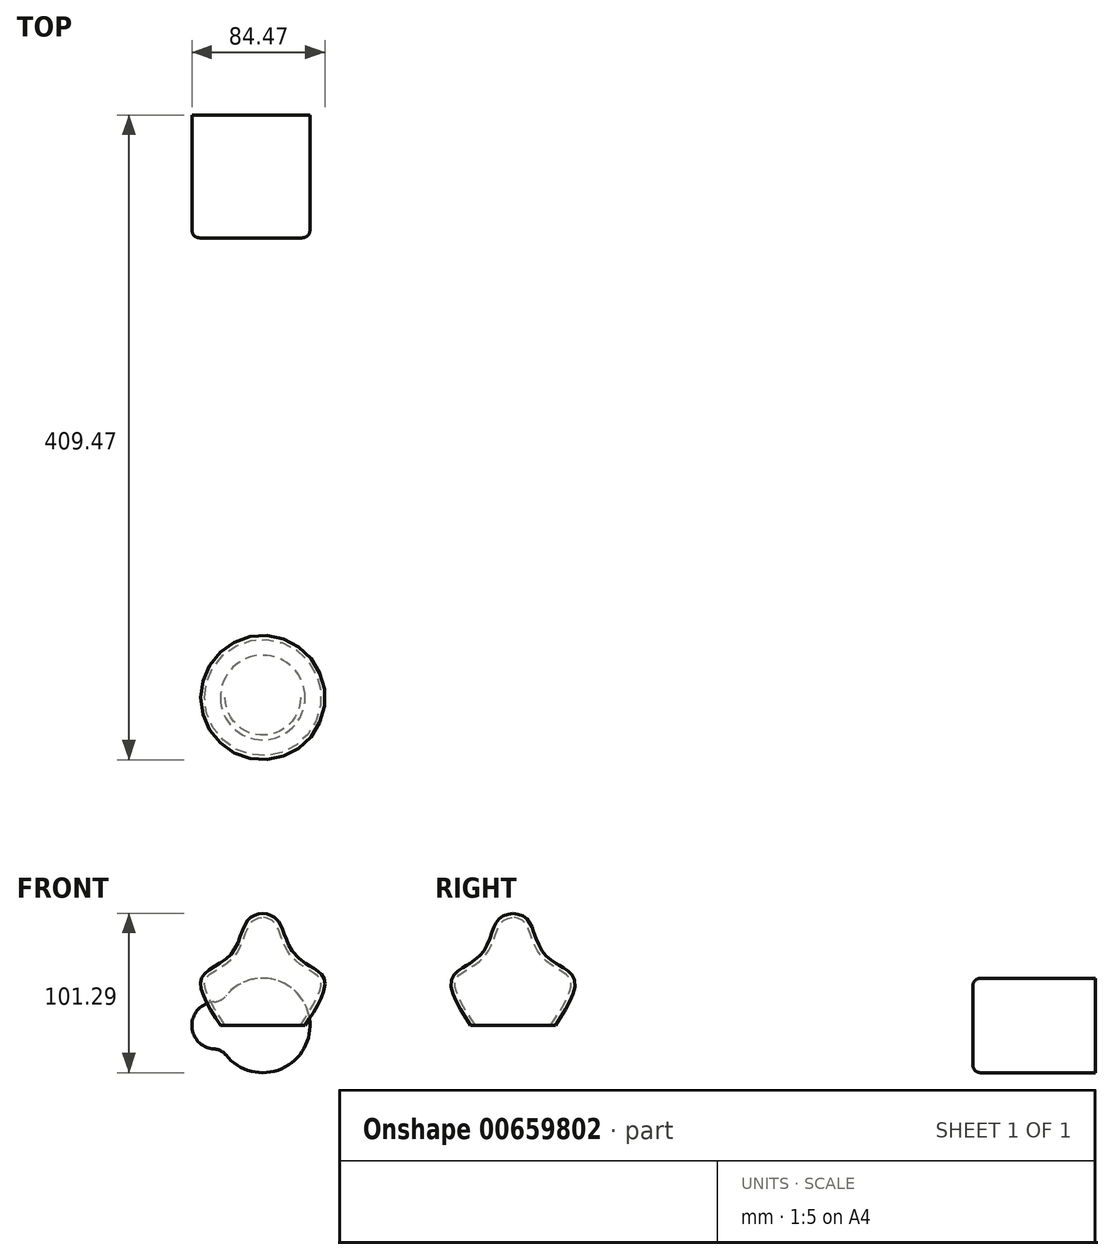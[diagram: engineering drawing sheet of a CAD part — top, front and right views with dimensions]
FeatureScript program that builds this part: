
annotation { "Feature Type Name" : "Feature", "Feature Type Description" : "" }
export const myFeature = defineFeature(function(context is Context, id is Id, definition is map)
    precondition{}
    {
        {
            var Q0;
            Q0=qCreatedBy(makeId("Front.planeOp"),FACE);
            var sketch = newSketch(context, id + "F0", { "sketchPlane" : qUnion([Q0])});
            skArc(sketch, "E0", {"start": v(-23.44, -18.73) * mm, "mid": v(30, 0) * mm, "end": v(-23.44, 18.73) * mm});
            skArc(sketch, "E1", {"start": v(-30.75, 14.98) * mm, "mid": v(-45, 0) * mm, "end": v(-30.75, -14.98) * mm});
            skPoint(sketch, "E2.visualSharp", {"position": v(-26.25, 14.52) * mm});
            skArc(sketch, "E2.filletArc", {"start": v(-30.75, 14.98) * mm, "mid": v(-26.7, 16.07) * mm, "end": v(-23.44, 18.73) * mm});
            skPoint(sketch, "E3.visualSharp", {"position": v(-26.25, -14.52) * mm});
            skArc(sketch, "E3.filletArc", {"start": v(-23.44, -18.73) * mm, "mid": v(-26.7, -16.07) * mm, "end": v(-30.75, -14.98) * mm});
            skSolve(sketch);
        }
        {
            var Q0;
            Q0=makeQuery(id+"F0.imprint","IMPRINT",FACE,{"disambiguationData":[TD([[makeQuery(id+"F0.imprint","IMPRINT",EDGE,{"derivedFrom":sQuery(id+"F0.wireOp",EDGE,"E0")}),1.0]])]});
            extrude(context, id + "F1", {"entities" : qUnion([Q0]), "oppositeDirection" : true, "depth" : 78 * mm, "offsetDistance" : 25 * mm});
        }
        {
            var Q0;
            Q0=makeQuery(id+"F1.opExtrude","CAP_EDGE",EDGE,{"disambiguationData":[OSD([sQuery(id+"F0.wireOp",EDGE,"E0")])],"isStart":true});
            fillet(context, id + "F2", {"entities" : qUnion([Q0]), "radius" : 5 * mm, "tangentPropagation" : true, "allowEdgeOverflow" : false});
        }
        {
            var Q0;
            Q0=qCreatedBy(makeId("Right.planeOp"),FACE);
            cPlane(context, id + "F3", {"entities" : qUnion([Q0]), "cplaneType" : CPlaneType.OFFSET, "offset" : 154 * mm, "width" : 150 * mm, "height" : 150 * mm});
        }
        {
            var Q0;
            Q0=qCreatedBy(id+"F3.planeOp",FACE);
            cPlane(context, id + "F4", {"entities" : qUnion([Q0]), "cplaneType" : CPlaneType.OFFSET, "offset" : 120 * mm, "width" : 150 * mm, "height" : 150 * mm});
        }
        {
            var Q0;
            Q0=qCreatedBy(makeId("Front.planeOp"),FACE);
            cPlane(context, id + "F5", {"entities" : qUnion([Q0]), "cplaneType" : CPlaneType.OFFSET, "offset" : 292 * mm, "width" : 150 * mm, "height" : 150 * mm});
        }
        {
            var Q0;
            Q0=qCreatedBy(id+"F5.planeOp",FACE);
            var sketch = newSketch(context, id + "F6", { "sketchPlane" : qUnion([Q0])});
            skFitSpline(sketch, "E4", {"points": [v(-26.88, 0) * mm, v(-38.8, 30.05) * mm, v(-20.42, 44.96) * mm, v(-9.73, 66.57) * mm, v(0, 71.3) * mm], "startDerivative": vector(-73.65, 114.28) * mm, "endDerivative": vector(61.92, 12.77) * mm});
            skLineSegment(sketch, "E5", {"start": v(0, 71.3) * mm, "end": v(0, 0) * mm});
            skLineSegment(sketch, "E6", {"start": v(0, 0) * mm, "end": v(-26.88, 0) * mm});
            skLineSegment(sketch, "E7", {"start": v(0, 0) * mm, "end": v(0, -43.5) * mm, "construction": true});
            skSolve(sketch);
        }
        {
            var Q0;
            Q0=makeQuery(id+"F6.imprint","IMPRINT",FACE,{"disambiguationData":[TD([[makeQuery(id+"F6.imprint","IMPRINT",EDGE,{"derivedFrom":sQuery(id+"F6.wireOp",EDGE,"E4")}),-1.0]])]});
            var Q1;
            Q1=sQuery(id+"F6.wireOp",EDGE,"E7");
            revolve(context, id + "F7", {"entities" : qUnion([Q0]), "axis" : qUnion([Q1]), "revolveType" : RevolveType.FULL});
        }
        {
            var Q0;
            Q0=makeQuery(id+"F7.opRevolve","SWEPT_FACE",FACE,{"disambiguationData":[OSD([sQuery(id+"F6.wireOp",EDGE,"E6")])]});
            shell(context, id + "F8", {"entities" : qUnion([Q0]), "thickness" : 2.5 * mm});
        }
    });
